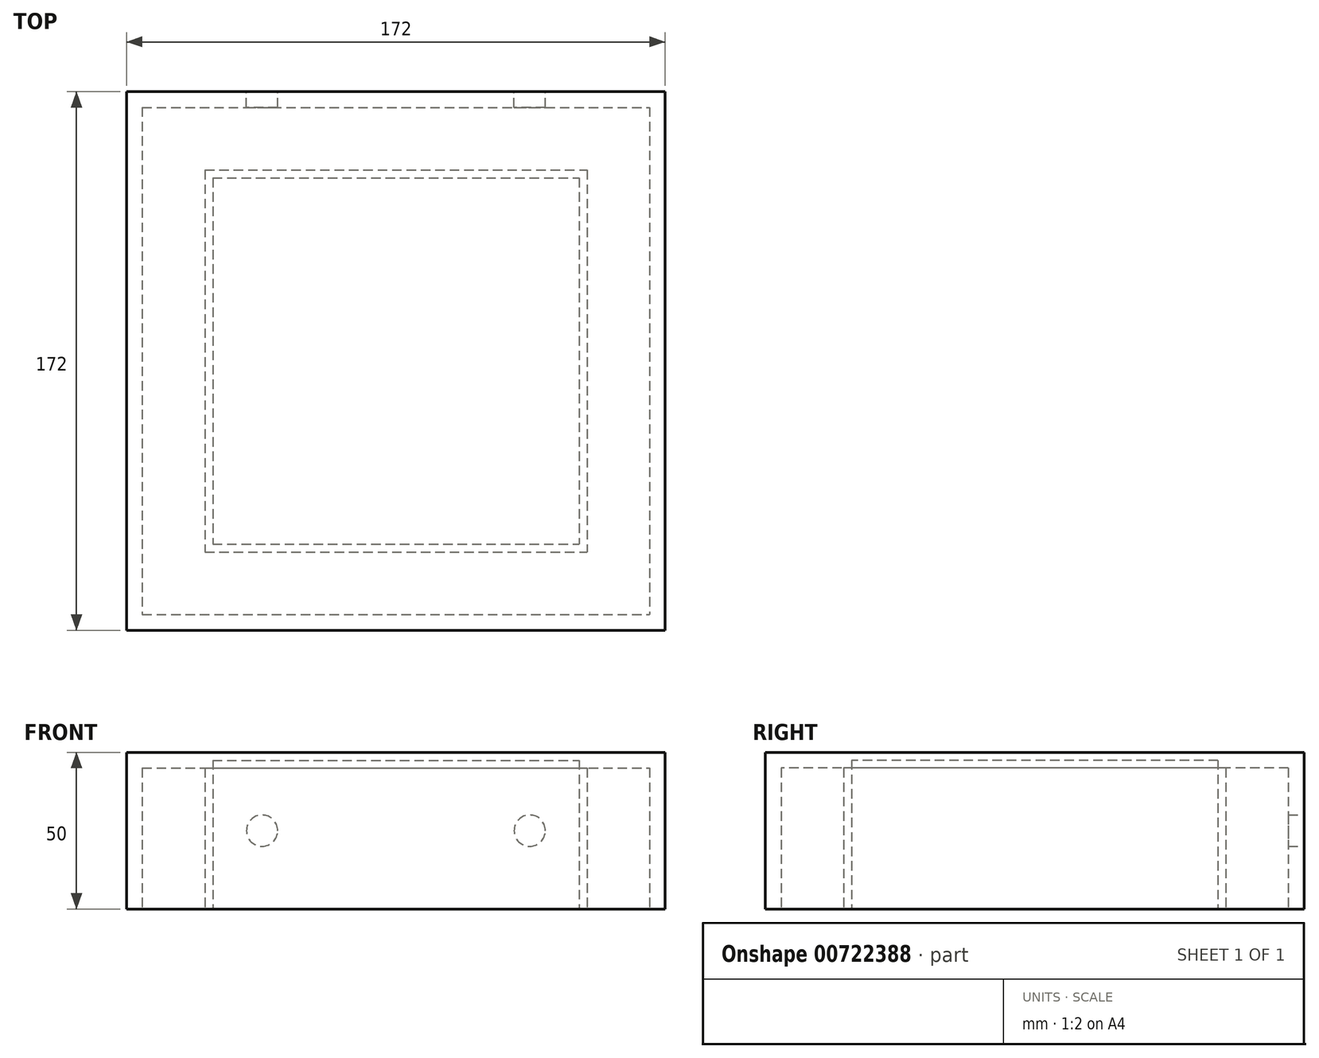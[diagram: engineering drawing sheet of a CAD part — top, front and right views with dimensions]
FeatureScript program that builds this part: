
annotation { "Feature Type Name" : "Feature", "Feature Type Description" : "" }
export const myFeature = defineFeature(function(context is Context, id is Id, definition is map)
    precondition{}
    {
        {
            var Q0;
            Q0=qCreatedBy(makeId("Top.planeOp"),FACE);
            var sketch = newSketch(context, id + "F0", { "sketchPlane" : qUnion([Q0])});
            skLineSegment(sketch, "E0.bottom", {"start": v(-86, 86) * mm, "end": v(86, 86) * mm});
            skLineSegment(sketch, "E0.top", {"start": v(-86, -86) * mm, "end": v(86, -86) * mm});
            skLineSegment(sketch, "E0.left", {"start": v(-86, 86) * mm, "end": v(-86, -86) * mm});
            skLineSegment(sketch, "E0.right", {"start": v(86, 86) * mm, "end": v(86, -86) * mm});
            skPoint(sketch, "E0.middle", {"position": v(0, 0) * mm});
            skSolve(sketch);
        }
        {
            var Q0;
            Q0 = qSketchRegion(id + "F0", true);
            extrude(context, id + "F1", {"entities" : qUnion([Q0]), "depth" : 50 * mm, "offsetDistance" : 25 * mm});
        }
        {
            var Q0;
            Q0=qCreatedBy(makeId("Top.planeOp"),FACE);
            var sketch = newSketch(context, id + "F2", { "sketchPlane" : qUnion([Q0])});
            skLineSegment(sketch, "E1.bottom", {"start": v(-81, 81) * mm, "end": v(81, 81) * mm});
            skLineSegment(sketch, "E1.top", {"start": v(-81, -81) * mm, "end": v(81, -81) * mm});
            skLineSegment(sketch, "E1.left", {"start": v(-81, 81) * mm, "end": v(-81, -81) * mm});
            skLineSegment(sketch, "E1.right", {"start": v(81, 81) * mm, "end": v(81, -81) * mm});
            skPoint(sketch, "E1.middle", {"position": v(0, 0) * mm});
            skLineSegment(sketch, "E2.bottom", {"start": v(-61, 61) * mm, "end": v(61, 61) * mm});
            skLineSegment(sketch, "E2.top", {"start": v(-61, -61) * mm, "end": v(61, -61) * mm});
            skLineSegment(sketch, "E2.left", {"start": v(-61, 61) * mm, "end": v(-61, -61) * mm});
            skLineSegment(sketch, "E2.right", {"start": v(61, 61) * mm, "end": v(61, -61) * mm});
            skSolve(sketch);
        }
        {
            var Q0;
            Q0 = qSketchRegion(id + "F2", true);
            extrude(context, id + "F3", {"entities" : qUnion([Q0]), "operationType" : NewBodyOperationType.REMOVE, "depth" : 45 * mm, "offsetDistance" : 25 * mm});
        }
        {
            var Q0;
            Q0=makeQuery(id+"F3.boolean.opBoolean","SPLIT",FACE,{"disambiguationData":[TD([makeQuery(id+"F3.opExtrude","SWEPT_FACE",FACE,{"disambiguationData":[OSD([sQuery(id+"F2.wireOp",EDGE,"E2.bottom")])]})])],"derivedFrom":makeQuery(id+"F1.opExtrude","CAP_FACE",FACE,{"disambiguationData":[OSD([sQuery(id+"F0.wireOp",EDGE,"E0.bottom"),sQuery(id+"F0.wireOp",EDGE,"E0.top"),sQuery(id+"F0.wireOp",EDGE,"E0.left"),sQuery(id+"F0.wireOp",EDGE,"E0.right")])],"isStart":true})});
            shell(context, id + "F4", {"entities" : qUnion([Q0]), "thickness" : 2.5 * mm});
        }
        {
            var Q0;
            Q0=makeQuery(id+"F1.opExtrude","SWEPT_FACE",FACE,{"disambiguationData":[OSD([sQuery(id+"F0.wireOp",EDGE,"E0.bottom")])]});
            var sketch = newSketch(context, id + "F5", { "sketchPlane" : qUnion([Q0])});
            skCircle(sketch, "E3", {"center": v(42.74, 25) * mm, "radius": 5 * mm});
            skCircle(sketch, "E4.MirrorC", {"center": v(-42.74, 25) * mm, "radius": 5 * mm});
            skSolve(sketch);
        }
        {
            var Q0;
            Q0 = qSketchRegion(id + "F5", true);
            extrude(context, id + "F6", {"entities" : qUnion([Q0]), "operationType" : NewBodyOperationType.REMOVE, "oppositeDirection" : true, "depth" : 9.5 * mm, "offsetDistance" : 25 * mm});
        }
    });
